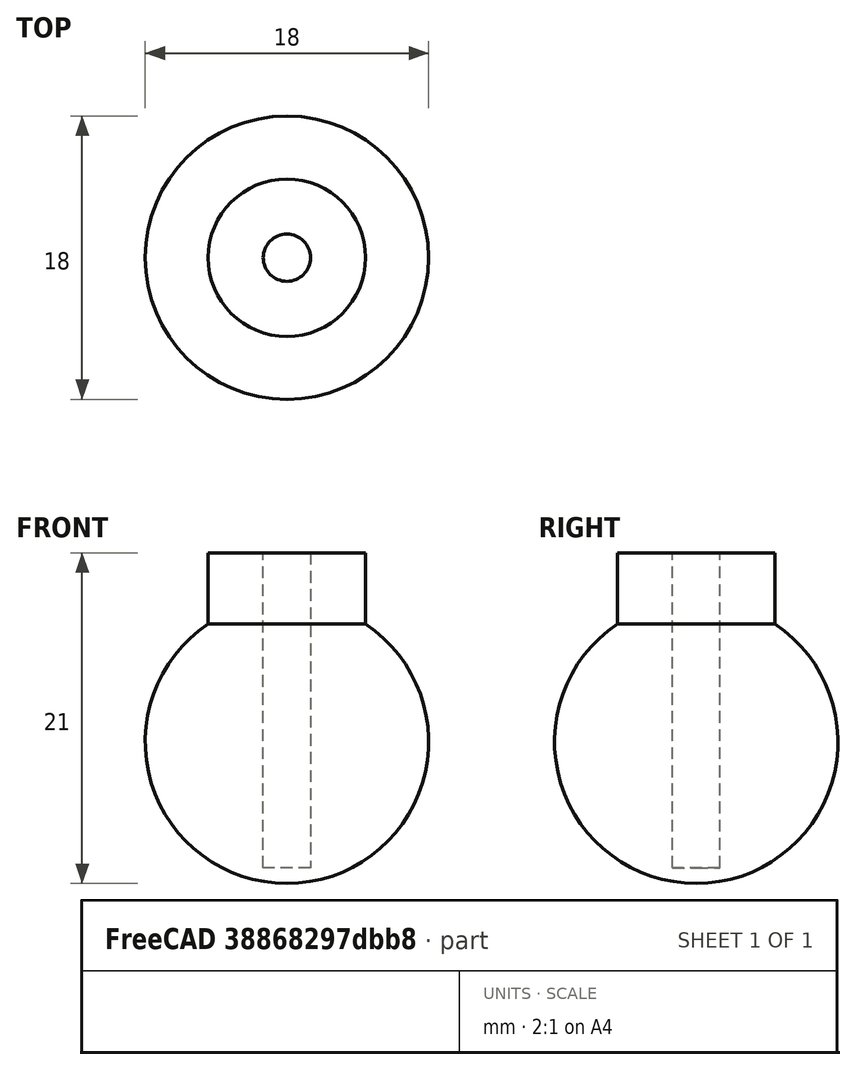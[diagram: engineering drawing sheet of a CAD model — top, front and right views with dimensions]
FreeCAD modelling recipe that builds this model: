
FCSTD DOCUMENT  (FreeCAD 0.15R4671 (Git))
Label: v4 charging handle
License: All rights reserved
LicenseURL: http://en.wikipedia.org/wiki/All_rights_reserved
objects: Part::Cylinder×1, Part::Sphere×1, Part::MultiFuse×1, Sketcher::SketchObject×1, PartDesign::Pocket×1
note: 6 computed .brp shape members not serialized (recipe doc carries the construction recipe); baked Part::Feature solids carry a one-line shape summary decoded from their .brp

FEATURE [Part::Cylinder] Cylinder
  Angle = 360
  Height = 7
  Radius = 5
FEATURE [Part::Sphere] Sphere
  Angle1 = -90
  Angle2 = 90
  Angle3 = 360
  Placement = pos=(0,0,-5) rot=(0,0,1;0rad)
  Radius = 9
FEATURE [Part::MultiFuse] Fusion
  Shapes = -> [Cylinder,Sphere]
FEATURE [Sketcher::SketchObject] Sketch
  Placement = pos=(0,0,7) rot=(0,0,1;0rad)
  Support = -> Fusion [Face1]
  sketch-geometry (1):
    g0: Circle CenterX=0 CenterY=0 CenterZ=0 NormalX=0 NormalY=0 NormalZ=1 Radius=1.5
  constraints (2):
    c: Coincident(g0,g-1)
    c: Radius(g0) = 1.5
FEATURE [PartDesign::Pocket] Pocket
  Length = 20
  Sketch = -> Sketch
  Type = 0
